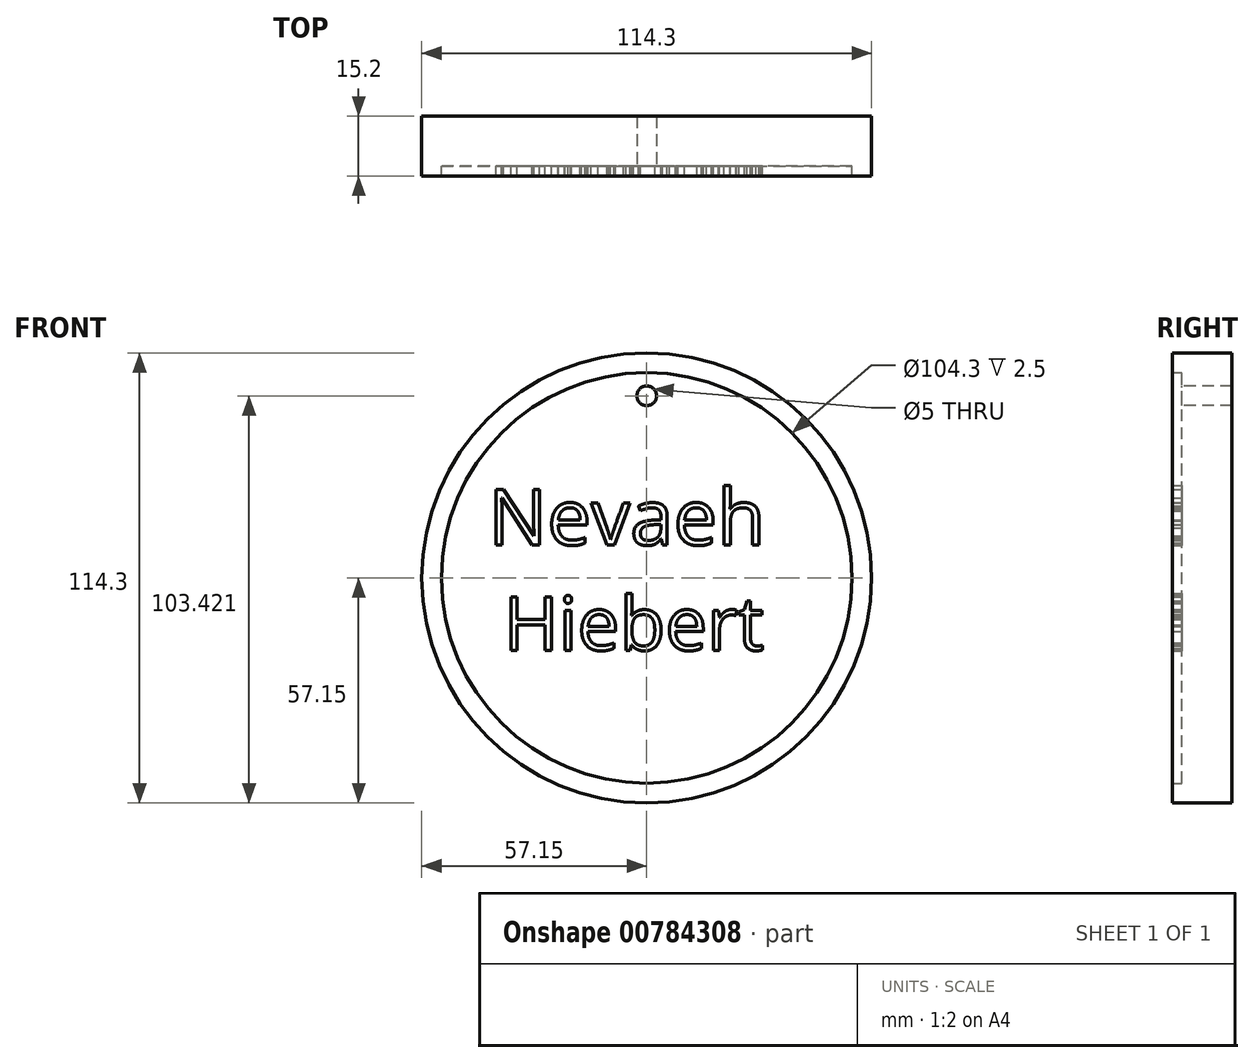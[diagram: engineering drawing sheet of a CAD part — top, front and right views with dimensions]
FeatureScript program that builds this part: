
annotation { "Feature Type Name" : "Feature", "Feature Type Description" : "" }
export const myFeature = defineFeature(function(context is Context, id is Id, definition is map)
    precondition{}
    {
        {
            var Q0;
            Q0=qCreatedBy(makeId("Front.planeOp"),FACE);
            var sketch = newSketch(context, id + "F0", { "sketchPlane" : qUnion([Q0])});
            skCircle(sketch, "E0", {"center": v(0, 0) * mm, "radius": 57.15 * mm});
            skSolve(sketch);
        }
        {
            var Q0;
            Q0 = qSketchRegion(id + "F0", true);
            extrude(context, id + "F1", {"entities" : qUnion([Q0]), "depth" : 12.7 * mm, "offsetDistance" : 25.4 * mm, "symmetric" : true});
        }
        {
            var Q0;
            Q0=makeQuery(id+"F1.opExtrude","CAP_FACE",FACE,{"disambiguationData":[OSD([sQuery(id+"F0.wireOp",EDGE,"E0")])],"isStart":false});
            var sketch = newSketch(context, id + "F2", { "sketchPlane" : qUnion([Q0])});
            skSolve(sketch);
        }
        {
            var Q0;
            Q0=makeQuery(id+"F2.imprint","IMPRINT",FACE,{"disambiguationData":[TD([[makeQuery(id+"F2.imprint","IMPRINT",EDGE,{"derivedFrom":makeQuery(id+"F1.opExtrude","CAP_EDGE",EDGE,{"disambiguationData":[OSD([sQuery(id+"F0.wireOp",EDGE,"E0")])],"isStart":false})}),1.0]])]});
            var sketch = newSketch(context, id + "F3", { "sketchPlane" : qUnion([Q0])});
            skCircle(sketch, "E1.0", {"center": v(0, 0) * mm, "radius": 52.15 * mm});
            skSolve(sketch);
        }
        {
            var Q0;
            Q0=makeQuery(id+"F3.imprint","IMPRINT",FACE,{"disambiguationData":[TD([[makeQuery(id+"F3.imprint","IMPRINT",EDGE,{"derivedFrom":sQuery(id+"F3.wireOp",EDGE,"E1.0")}),-1.0]])]});
            extrude(context, id + "F4", {"entities" : qUnion([Q0]), "operationType" : NewBodyOperationType.ADD, "depth" : 2.5 * mm, "offsetDistance" : 25 * mm});
        }
        {
            var Q0;
            Q0=makeQuery(id+"F2.imprint","IMPRINT",FACE,{"disambiguationData":[TD([[makeQuery(id+"F2.imprint","IMPRINT",EDGE,{"derivedFrom":makeQuery(id+"F1.opExtrude","CAP_EDGE",EDGE,{"disambiguationData":[OSD([sQuery(id+"F0.wireOp",EDGE,"E0")])],"isStart":false})}),1.0]])]});
            var sketch = newSketch(context, id + "F5", { "sketchPlane" : qUnion([Q0])});
            skText(sketch, "E2", { "text": "Nevaeh", "fontName": "OpenSans-Regular.ttf"});
            const initialGuessF5  = {"E2": [-0.0402, 0.00838, 1, 0, 0.01427]};
            skSetInitialGuess(sketch, initialGuessF5);
            skSolve(sketch);
        }
        {
            var Q0;
            Q0=makeQuery(id+"F2.imprint","IMPRINT",FACE,{"disambiguationData":[TD([[makeQuery(id+"F2.imprint","IMPRINT",EDGE,{"derivedFrom":makeQuery(id+"F1.opExtrude","CAP_EDGE",EDGE,{"disambiguationData":[OSD([sQuery(id+"F0.wireOp",EDGE,"E0")])],"isStart":false})}),1.0]])]});
            var sketch = newSketch(context, id + "F6", { "sketchPlane" : qUnion([Q0])});
            skText(sketch, "E3", { "text": "Hiebert\n", "fontName": "OpenSans-Regular.ttf"});
            const initialGuessF6  = {"E3": [-0.0364, -0.01837, 1, 0, 0.01367]};
            skSetInitialGuess(sketch, initialGuessF6);
            skSolve(sketch);
        }
        {
            var Q0;
            Q0=makeQuery(id+"F2.imprint","IMPRINT",FACE,{"disambiguationData":[TD([[makeQuery(id+"F2.imprint","IMPRINT",EDGE,{"derivedFrom":makeQuery(id+"F1.opExtrude","CAP_EDGE",EDGE,{"disambiguationData":[OSD([sQuery(id+"F0.wireOp",EDGE,"E0")])],"isStart":false})}),1.0]])]});
            var sketch = newSketch(context, id + "F7", { "sketchPlane" : qUnion([Q0])});
            skCircle(sketch, "E4", {"center": v(0, 46.27) * mm, "radius": 4.2 * mm});
            skSolve(sketch);
        }
        {
            var Q0;
            Q0=sQuery(id+"F7.wireOp",VERTEX,"E4.center");
            var Q1;
            Q1=makeQuery(id+"F1.opExtrude","SWEPT_BODY",BODY,{"disambiguationData":[OSD([sQuery(id+"F0.wireOp",EDGE,"E0")])]});
            hole(context, id + "F8", {"style" : HoleStyle.SIMPLE, "endStyle" : HoleEndStyle.THROUGH, "holeDiameter" : 5 * mm, "majorDiameter" : 5 * mm, "isTappedThrough" : true, "tappedDepth" : 12 * mm, "tapClearance" : 3, "locations" : qUnion([Q0]), "scope" : qUnion([Q1])});
        }
        {
            var Q0;
            Q0 = qSketchRegion(id + "F5", true);
            extrude(context, id + "F9", {"entities" : qUnion([Q0]), "operationType" : NewBodyOperationType.ADD, "depth" : 2.5 * mm, "offsetDistance" : 25 * mm});
        }
        {
            var Q0;
            Q0 = qSketchRegion(id + "F6", true);
            extrude(context, id + "F10", {"entities" : qUnion([Q0]), "operationType" : NewBodyOperationType.ADD, "depth" : 2.5 * mm, "offsetDistance" : 25 * mm});
        }
    });
